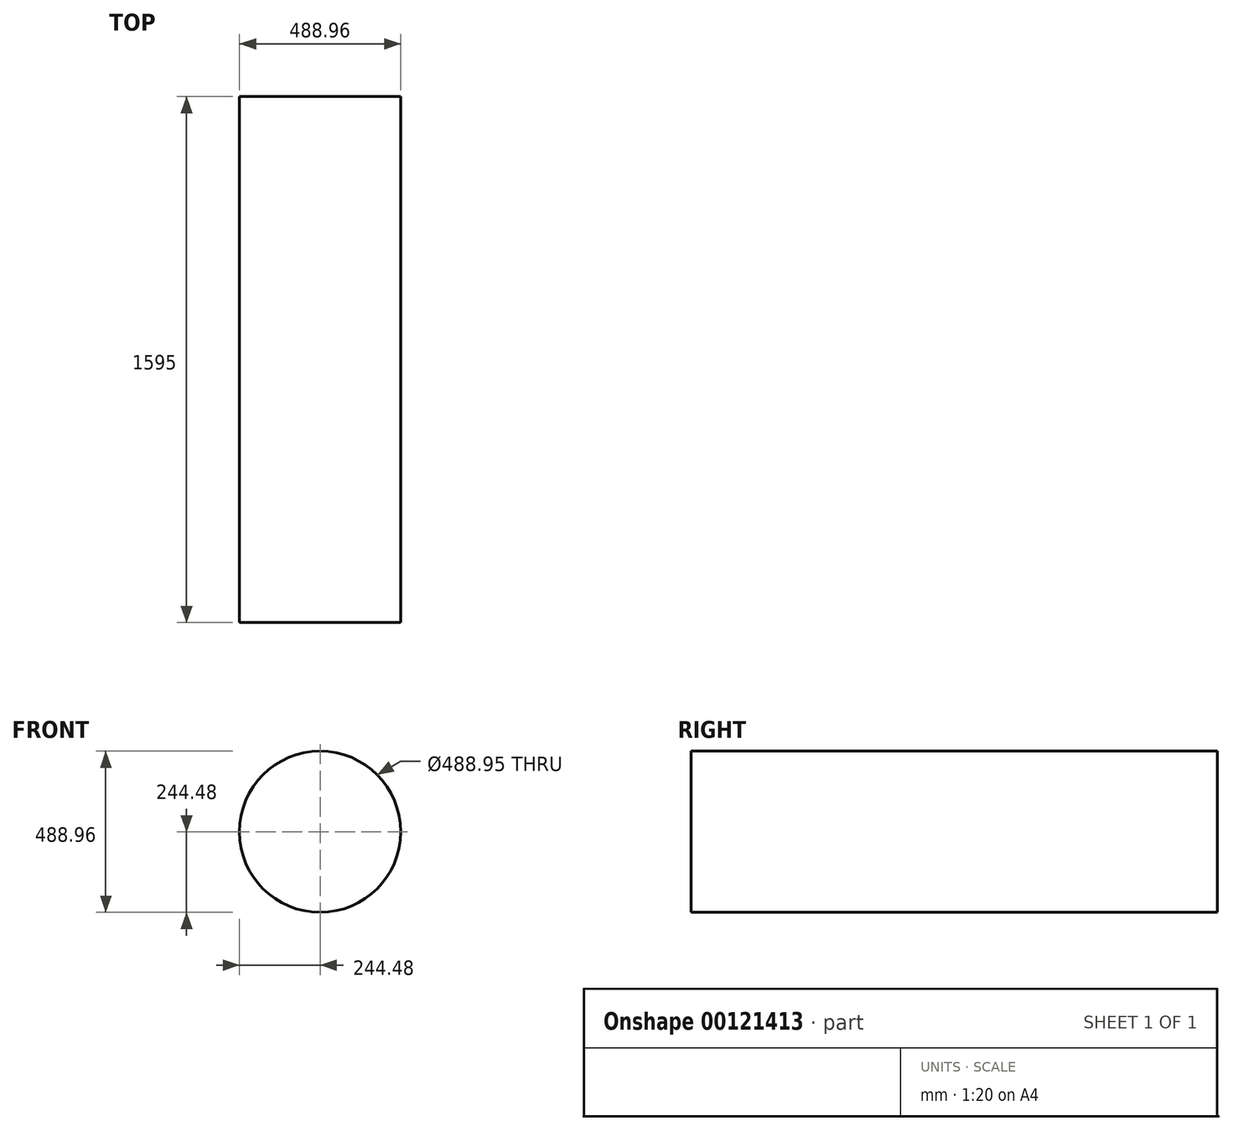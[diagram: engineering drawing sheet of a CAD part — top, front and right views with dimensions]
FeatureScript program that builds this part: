
annotation { "Feature Type Name" : "Feature", "Feature Type Description" : "" }
export const myFeature = defineFeature(function(context is Context, id is Id, definition is map)
    precondition{}
    {
        {
            var Q0;
            Q0=qCreatedBy(makeId("Front.planeOp"),FACE);
            var sketch = newSketch(context, id + "F0", { "sketchPlane" : qUnion([Q0])});
            skCircle(sketch, "E0", {"center": v(0, 0) * mm, "radius": 244.47 * mm});
            skLineSegment(sketch, "E1", {"start": v(0, 0) * mm, "end": v(0, 244.47) * mm});
            skSolve(sketch);
        }
        {
            var Q0;
            Q0=sQuery(id+"F0.wireOp",EDGE,"E0");
            extrude(context, id + "F1", {"bodyType" : ToolBodyType.SURFACE, "surfaceEntities" : qUnion([Q0]), "oppositeDirection" : true, "depth" : 395 * mm, "hasSecondDirection" : true, "secondDirectionOppositeDirection" : false, "secondDirectionDepth" : 1200 * mm});
        }
    });
